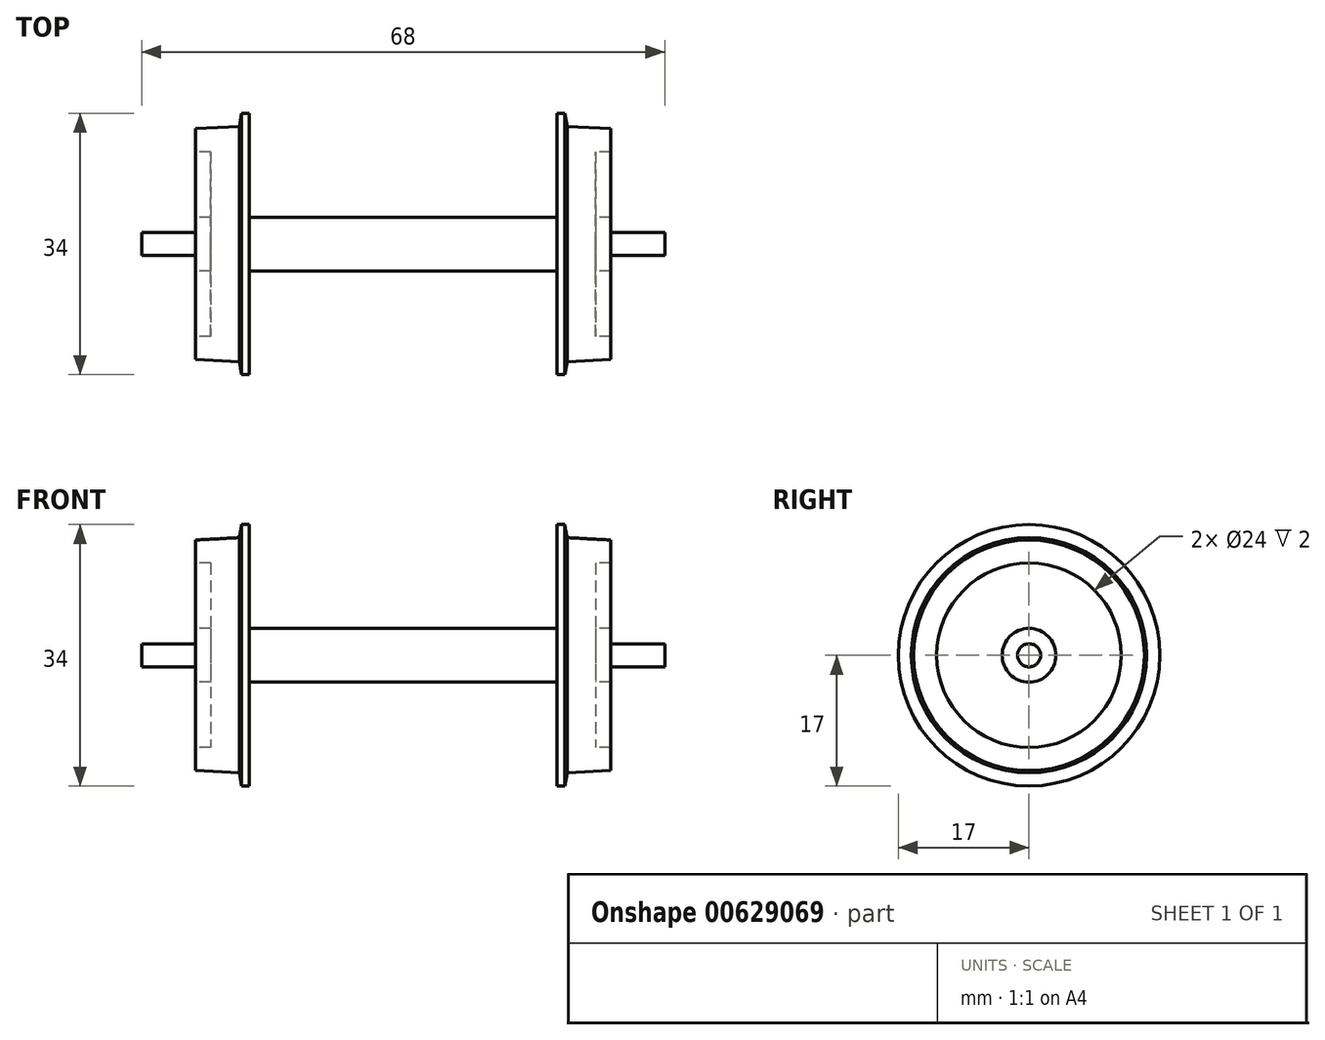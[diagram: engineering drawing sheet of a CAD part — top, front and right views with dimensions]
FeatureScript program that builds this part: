
annotation { "Feature Type Name" : "Feature", "Feature Type Description" : "" }
export const myFeature = defineFeature(function(context is Context, id is Id, definition is map)
    precondition{}
    {
        {
            var Q0;
            Q0=qCreatedBy(makeId("Top.planeOp"),FACE);
            var sketch = newSketch(context, id + "F0", { "sketchPlane" : qUnion([Q0])});
            skLineSegment(sketch, "E0", {"start": v(-71, 0) * mm, "end": v(71.98, 0) * mm, "construction": true});
            skLineSegment(sketch, "E1", {"start": v(0, 33.1) * mm, "end": v(0, -34.08) * mm, "construction": true});
            skLineSegment(sketch, "E2", {"start": v(27, 12) * mm, "end": v(27, 15) * mm});
            skLineSegment(sketch, "E3", {"start": v(27, 15) * mm, "end": v(21.3, 15.3) * mm});
            skLineSegment(sketch, "E4", {"start": v(21.3, 15.3) * mm, "end": v(21, 17) * mm});
            skLineSegment(sketch, "E5", {"start": v(21, 17) * mm, "end": v(20, 17) * mm});
            skLineSegment(sketch, "E6", {"start": v(20, 17) * mm, "end": v(20, 3.5) * mm});
            skLineSegment(sketch, "E7", {"start": v(20, 3.5) * mm, "end": v(0, 3.5) * mm});
            skLineSegment(sketch, "E8", {"start": v(27, 12) * mm, "end": v(25, 12) * mm});
            skLineSegment(sketch, "E9", {"start": v(25, 12) * mm, "end": v(25, 3.5) * mm});
            skLineSegment(sketch, "E10", {"start": v(34, 0) * mm, "end": v(34, 1.5) * mm});
            skLineSegment(sketch, "E11", {"start": v(34, 1.5) * mm, "end": v(27, 1.5) * mm});
            skLineSegment(sketch, "E12", {"start": v(27, 1.5) * mm, "end": v(27, 3.5) * mm});
            skLineSegment(sketch, "E13", {"start": v(27, 3.5) * mm, "end": v(25, 3.5) * mm});
            skLineSegment(sketch, "E14.MirrorCS", {"start": v(-27, 12) * mm, "end": v(-27, 15) * mm});
            skLineSegment(sketch, "E15.MirrorCS", {"start": v(-27, 12) * mm, "end": v(-25, 12) * mm});
            skLineSegment(sketch, "E16.MirrorCS", {"start": v(-27, 3.5) * mm, "end": v(-25, 3.5) * mm});
            skLineSegment(sketch, "E17.MirrorCS", {"start": v(-21, 17) * mm, "end": v(-20, 17) * mm});
            skLineSegment(sketch, "E18.MirrorCS", {"start": v(-21.3, 15.3) * mm, "end": v(-21, 17) * mm});
            skLineSegment(sketch, "E19.MirrorCS", {"start": v(-20, 17) * mm, "end": v(-20, 3.5) * mm});
            skLineSegment(sketch, "E20.MirrorCS", {"start": v(-25, 12) * mm, "end": v(-25, 3.5) * mm});
            skLineSegment(sketch, "E21.MirrorCS", {"start": v(-27, 15) * mm, "end": v(-21.3, 15.3) * mm});
            skLineSegment(sketch, "E22.MirrorCS", {"start": v(-27, 1.5) * mm, "end": v(-27, 3.5) * mm});
            skLineSegment(sketch, "E23.MirrorCS", {"start": v(-34, 1.5) * mm, "end": v(-27, 1.5) * mm});
            skLineSegment(sketch, "E24.MirrorCS", {"start": v(-34, 0) * mm, "end": v(-34, 1.5) * mm});
            skLineSegment(sketch, "E25.MirrorCS", {"start": v(-20, 3.5) * mm, "end": v(0, 3.5) * mm});
            skLineSegment(sketch, "E26", {"start": v(-34, 0) * mm, "end": v(34, 0) * mm});
            skSolve(sketch);
        }
        {
            var Q0;
            Q0 = qSketchRegion(id + "F0", true);
            var Q1;
            Q1=sQuery(id+"F0.wireOp",EDGE,"E0");
            revolve(context, id + "F1", {"entities" : qUnion([Q0]), "axis" : qUnion([Q1]), "revolveType" : RevolveType.FULL});
        }
    });
